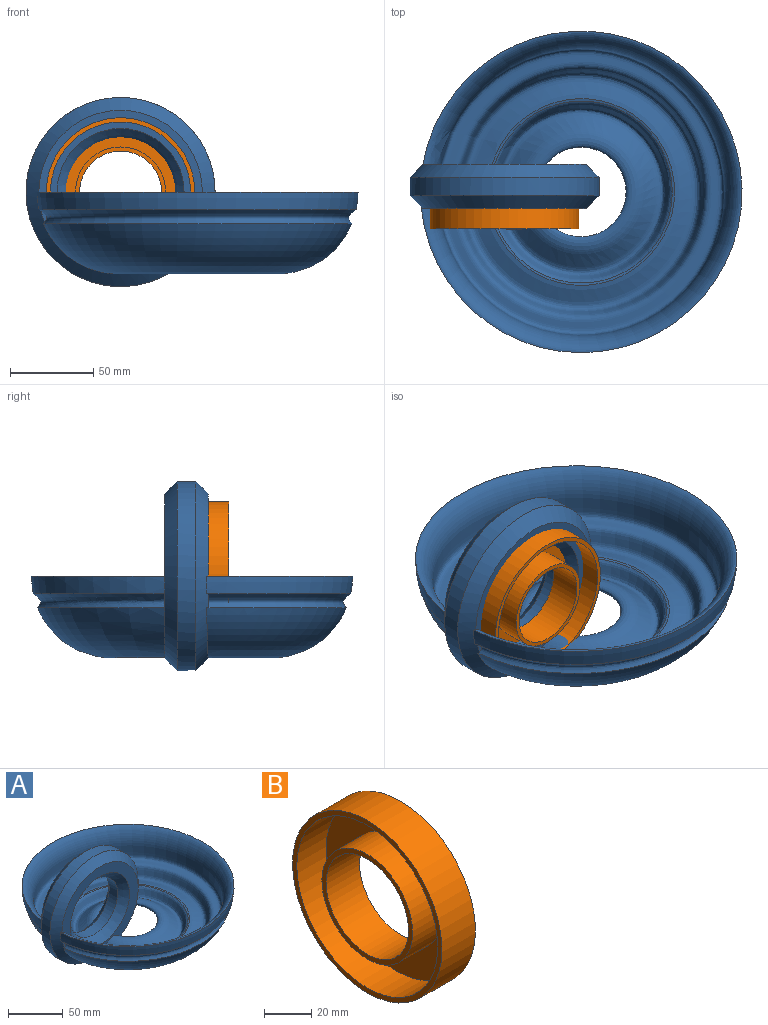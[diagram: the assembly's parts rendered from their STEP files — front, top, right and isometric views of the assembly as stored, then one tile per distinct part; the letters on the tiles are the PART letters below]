
ASSEMBLY  parts=2 mates=1
PART A: 16 faces, bbox 199.6x192.9x113.7 mm
  f0: plane 8.84x5.04mm, normal (0,1,0), area 17.4mm2, adj f5,f12
  f1: plane 6.82x3.48mm, normal (0,-1,0), area 10.2mm2, adj f7,f12
  f2: cylinder r=30.46mm len=60.92mm, axis (0,1,0), area 2093.4mm2, adj f3,f9
  f3: cone r=38.19mm half-angle=45deg, axis (0,1,0), area 2359.2mm2, adj f2,f4,f14
  f4: plane 99x98.54mm, normal (0,1,0), area 2417.1mm2, adj f3,f5,f13,f15
  f5: cone r=56.87mm half-angle=45deg, axis (0,-1,0), area 3642.6mm2, adj f0,f4,f6,f10,f11
  f6: cylinder r=56.87mm len=113.73mm, axis (0,1,0), area 3908.4mm2, adj f5,f7
  f7: cone r=49.13mm half-angle=45deg, axis (0,1,0), area 3575.8mm2, adj f1,f6,f8,f10,f11,f12,f13
  f8: plane 98.28x98.27mm, normal (0,-1,0), area 2486mm2, adj f7,f9,f11,f13,f14,f15
  f9: cone r=30.46mm half-angle=45deg, axis (0,-1,0), area 2359.2mm2, adj f2,f8
  f10: revolved ~192.93x192.81mm, area 6178.1mm2, adj f5,f7,f12,f13
  f11: revolved ~185.45x185.26mm, area 26707.2mm2, adj f5,f7,f8,f12,f15
  f12: revolved ~190.67x190.53mm, area 6066.6mm2, adj f0,f1,f7,f10,f11
  f13: revolved ~192.93x192.81mm, area 32830.7mm2, adj f4,f7,f8,f10,f14
  f14: revolved ~112.13x111.24mm, area 457.9mm2, adj f3,f8,f13,f15
  f15: revolved ~109.33x108.42mm, area 11869.7mm2, adj f4,f8,f11,f14
PART B: 8 faces, bbox 20x89.2x89.2 mm
  f0: plane 54.22x54.22mm, normal (-1,0,0), area 406.2mm2, adj f3,f6
  f1: cylinder r=44.61mm len=89.22mm, axis (-1,0,0), area 5605.6mm2, adj f2,f4
  f2: plane 89.22x89.22mm, normal (-1,0,0), area 681.1mm2, adj f1,f5
  f3: cylinder r=24.61mm len=49.22mm, axis (-1,0,0), area 3092.3mm2, adj f0,f4
  f4: plane 89.22x89.22mm, normal (1,0,0), area 4348.9mm2, adj f1,f3
  f5: cylinder r=42.11mm len=84.22mm, axis (-1,0,0), area 4630mm2, adj f2,f7
  f6: cylinder r=27.11mm len=54.22mm, axis (-1,0,0), area 2980.6mm2, adj f0,f7
  f7: plane 84.22x84.22mm, normal (-1,0,0), area 3261.7mm2, adj f5,f6
PLACE A t=(-119.17,-117.23,-139.32)mm
PLACE B rot(axis=(0.71,0.71,0),180deg) t=(-119.17,-97.67,-139.32)mm
MATE ball B.f1 <-> A.f2  axis (0,1,0) through (-119.17,-122.7,-139.32)mm
